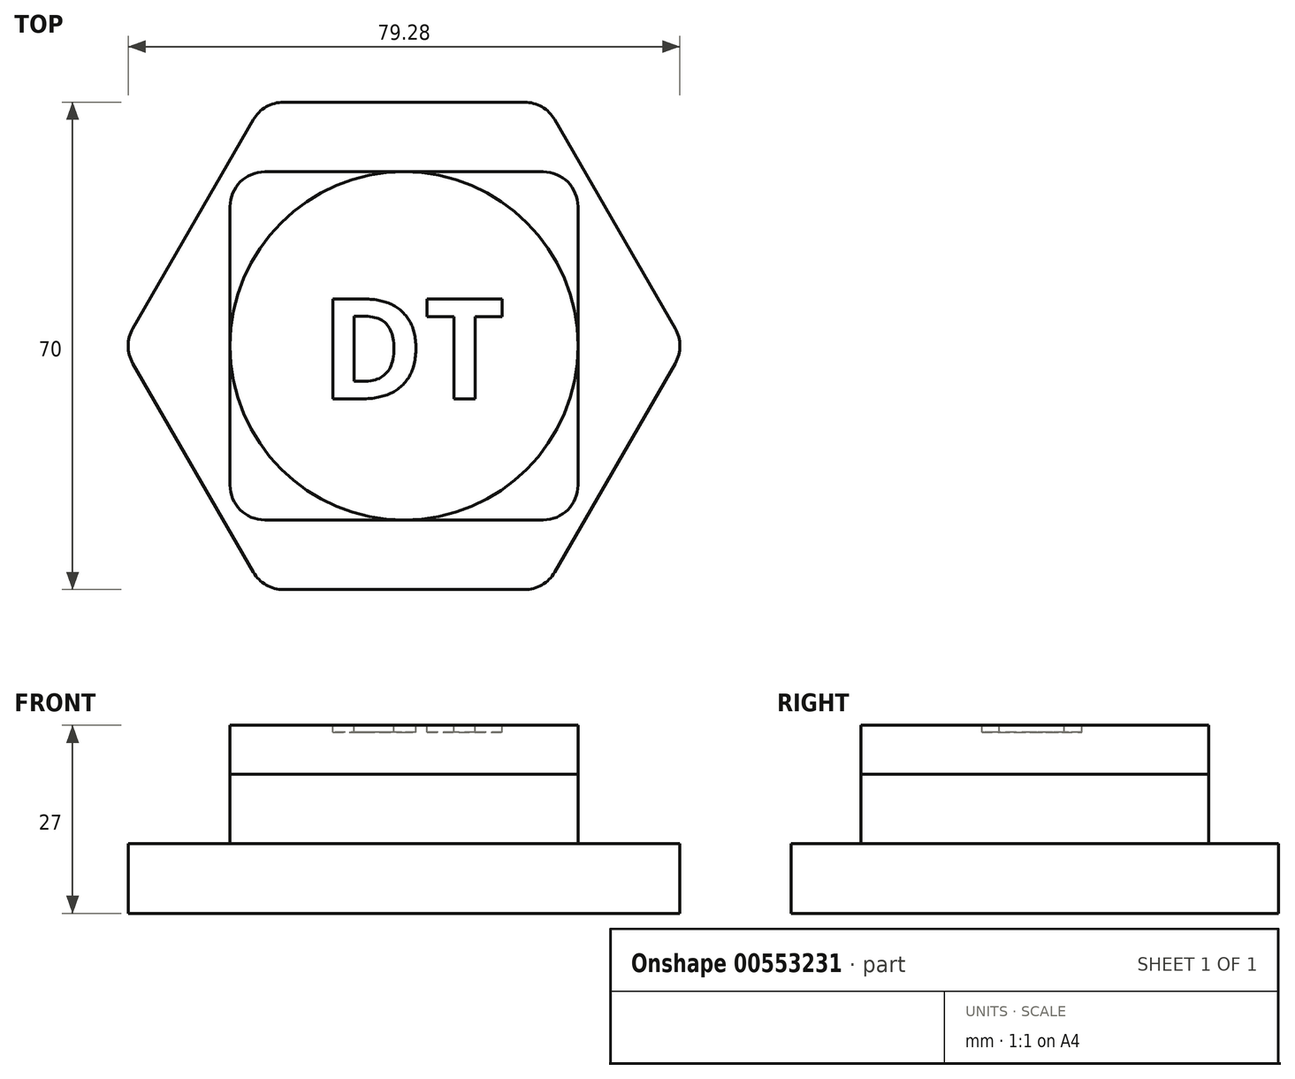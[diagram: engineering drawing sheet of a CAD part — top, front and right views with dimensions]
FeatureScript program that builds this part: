
annotation { "Feature Type Name" : "Feature", "Feature Type Description" : "" }
export const myFeature = defineFeature(function(context is Context, id is Id, definition is map)
    precondition{}
    {
        {
            var Q0;
            Q0=qCreatedBy(makeId("Top.planeOp"),FACE);
            var sketch = newSketch(context, id + "F0", { "sketchPlane" : qUnion([Q0])});
            skCircle(sketch, "E0.cCircle", {"center": v(0, 0) * mm, "radius": 35 * mm, "construction": true});
            skLineSegment(sketch, "E0.0", {"start": v(-20.2, 35) * mm, "end": v(20.2, 35) * mm});
            skLineSegment(sketch, "E0.1", {"start": v(20.2, 35) * mm, "end": v(40.41, 0) * mm});
            skLineSegment(sketch, "E0.2", {"start": v(40.41, 0) * mm, "end": v(20.2, -35) * mm});
            skLineSegment(sketch, "E0.3", {"start": v(20.2, -35) * mm, "end": v(-20.2, -35) * mm});
            skLineSegment(sketch, "E0.4", {"start": v(-20.2, -35) * mm, "end": v(-40.41, 0) * mm});
            skLineSegment(sketch, "E0.5", {"start": v(-40.41, 0) * mm, "end": v(-20.2, 35) * mm});
            skPoint(sketch, "E0.0.midPoint", {"position": v(0, 35) * mm});
            skSolve(sketch);
        }
        {
            var Q0;
            Q0=makeQuery(id+"F0.imprint","IMPRINT",FACE,{"disambiguationData":[TD([[makeQuery(id+"F0.imprint","IMPRINT",EDGE,{"derivedFrom":sQuery(id+"F0.wireOp",EDGE,"E0.0")}),-1.0]])]});
            extrude(context, id + "F1", {"entities" : qUnion([Q0]), "depth" : 10 * mm, "offsetDistance" : 25 * mm});
        }
        {
            var Q0;
            Q0=makeQuery(id+"F1.opExtrude","CAP_FACE",FACE,{"disambiguationData":[OSD([sQuery(id+"F0.wireOp",EDGE,"E0.0"),sQuery(id+"F0.wireOp",EDGE,"E0.1"),sQuery(id+"F0.wireOp",EDGE,"E0.2"),sQuery(id+"F0.wireOp",EDGE,"E0.3"),sQuery(id+"F0.wireOp",EDGE,"E0.4"),sQuery(id+"F0.wireOp",EDGE,"E0.5")])],"isStart":false});
            var sketch = newSketch(context, id + "F2", { "sketchPlane" : qUnion([Q0])});
            skLineSegment(sketch, "E1.bottom", {"start": v(-25, 25) * mm, "end": v(25, 25) * mm});
            skLineSegment(sketch, "E1.top", {"start": v(-25, -25) * mm, "end": v(25, -25) * mm});
            skLineSegment(sketch, "E1.left", {"start": v(-25, 25) * mm, "end": v(-25, -25) * mm});
            skLineSegment(sketch, "E1.right", {"start": v(25, 25) * mm, "end": v(25, -25) * mm});
            skPoint(sketch, "E1.middle", {"position": v(0, 0) * mm});
            skSolve(sketch);
        }
        {
            var Q0;
            Q0 = qSketchRegion(id + "F2", true);
            extrude(context, id + "F3", {"entities" : qUnion([Q0]), "operationType" : NewBodyOperationType.ADD, "depth" : 10 * mm, "offsetDistance" : 25 * mm});
        }
        {
            var Q0;
            Q0=makeQuery(id+"F1.opExtrude","SWEPT_EDGE",EDGE,{"disambiguationData":[OSD([sQuery(id+"F0.wireOp",EDGE,"E0.4"),sQuery(id+"F0.wireOp",EDGE,"E0.5")])]});
            var Q1;
            Q1=makeQuery(id+"F1.opExtrude","SWEPT_EDGE",EDGE,{"disambiguationData":[OSD([sQuery(id+"F0.wireOp",EDGE,"E0.3"),sQuery(id+"F0.wireOp",EDGE,"E0.4")])]});
            var Q2;
            Q2=makeQuery(id+"F1.opExtrude","SWEPT_EDGE",EDGE,{"disambiguationData":[OSD([sQuery(id+"F0.wireOp",EDGE,"E0.2"),sQuery(id+"F0.wireOp",EDGE,"E0.3")])]});
            var Q3;
            Q3=makeQuery(id+"F1.opExtrude","SWEPT_EDGE",EDGE,{"disambiguationData":[OSD([sQuery(id+"F0.wireOp",EDGE,"E0.1"),sQuery(id+"F0.wireOp",EDGE,"E0.2")])]});
            var Q4;
            Q4=makeQuery(id+"F1.opExtrude","SWEPT_EDGE",EDGE,{"disambiguationData":[OSD([sQuery(id+"F0.wireOp",EDGE,"E0.0"),sQuery(id+"F0.wireOp",EDGE,"E0.1")])]});
            var Q5;
            Q5=makeQuery(id+"F1.opExtrude","SWEPT_EDGE",EDGE,{"disambiguationData":[OSD([sQuery(id+"F0.wireOp",EDGE,"E0.0"),sQuery(id+"F0.wireOp",EDGE,"E0.5")])]});
            var Q6;
            Q6=makeQuery(id+"F3.opExtrude","SWEPT_EDGE",EDGE,{"disambiguationData":[OSD([sQuery(id+"F2.wireOp",EDGE,"E1.bottom"),sQuery(id+"F2.wireOp",EDGE,"E1.left")])]});
            var Q7;
            Q7=makeQuery(id+"F3.opExtrude","SWEPT_EDGE",EDGE,{"disambiguationData":[OSD([sQuery(id+"F2.wireOp",EDGE,"E1.top"),sQuery(id+"F2.wireOp",EDGE,"E1.left")])]});
            var Q8;
            Q8=makeQuery(id+"F3.opExtrude","SWEPT_EDGE",EDGE,{"disambiguationData":[OSD([sQuery(id+"F2.wireOp",EDGE,"E1.top"),sQuery(id+"F2.wireOp",EDGE,"E1.right")])]});
            var Q9;
            Q9=makeQuery(id+"F3.opExtrude","SWEPT_EDGE",EDGE,{"disambiguationData":[OSD([sQuery(id+"F2.wireOp",EDGE,"E1.bottom"),sQuery(id+"F2.wireOp",EDGE,"E1.right")])]});
            fillet(context, id + "F4", {"entities" : qUnion([Q0, Q1, Q2, Q3, Q4, Q5, Q6, Q7, Q8, Q9]), "radius" : 5 * mm, "tangentPropagation" : true, "allowEdgeOverflow" : false});
        }
        {
            var Q0;
            Q0=makeQuery(id+"F3.opExtrude","CAP_FACE",FACE,{"disambiguationData":[OSD([sQuery(id+"F2.wireOp",EDGE,"E1.bottom"),sQuery(id+"F2.wireOp",EDGE,"E1.top"),sQuery(id+"F2.wireOp",EDGE,"E1.left"),sQuery(id+"F2.wireOp",EDGE,"E1.right")])],"isStart":false});
            var sketch = newSketch(context, id + "F5", { "sketchPlane" : qUnion([Q0])});
            skCircle(sketch, "E2", {"center": v(0, 0) * mm, "radius": 25 * mm});
            skSolve(sketch);
        }
        {
            var Q0;
            Q0 = qSketchRegion(id + "F5", true);
            var Q1;
            Q1=sQuery(id+"F5.wireOp",EDGE,"E2");
            extrude(context, id + "F6", {"entities" : qUnion([Q0]), "surfaceEntities" : qUnion([Q1]), "depth" : 7 * mm, "offsetDistance" : 25 * mm});
        }
        {
            var Q0;
            Q0=makeQuery(id+"F6.opExtrude","CAP_FACE",FACE,{"disambiguationData":[OSD([sQuery(id+"F5.wireOp",EDGE,"E2")])],"isStart":false});
            var sketch = newSketch(context, id + "F7", { "sketchPlane" : qUnion([Q0])});
            skText(sketch, "E3", { "text": "DT", "fontName": "OpenSans-Bold.ttf"});
            const initialGuessF7  = {"E3": [-0.012, -0.00761, 1, 0, 0.01447]};
            skSetInitialGuess(sketch, initialGuessF7);
            skSolve(sketch);
        }
        {
            var Q0;
            Q0 = qSketchRegion(id + "F7", true);
            extrude(context, id + "F8", {"entities" : qUnion([Q0]), "operationType" : NewBodyOperationType.REMOVE, "oppositeDirection" : true, "depth" : 1 * mm, "offsetDistance" : 25 * mm});
        }
    });
